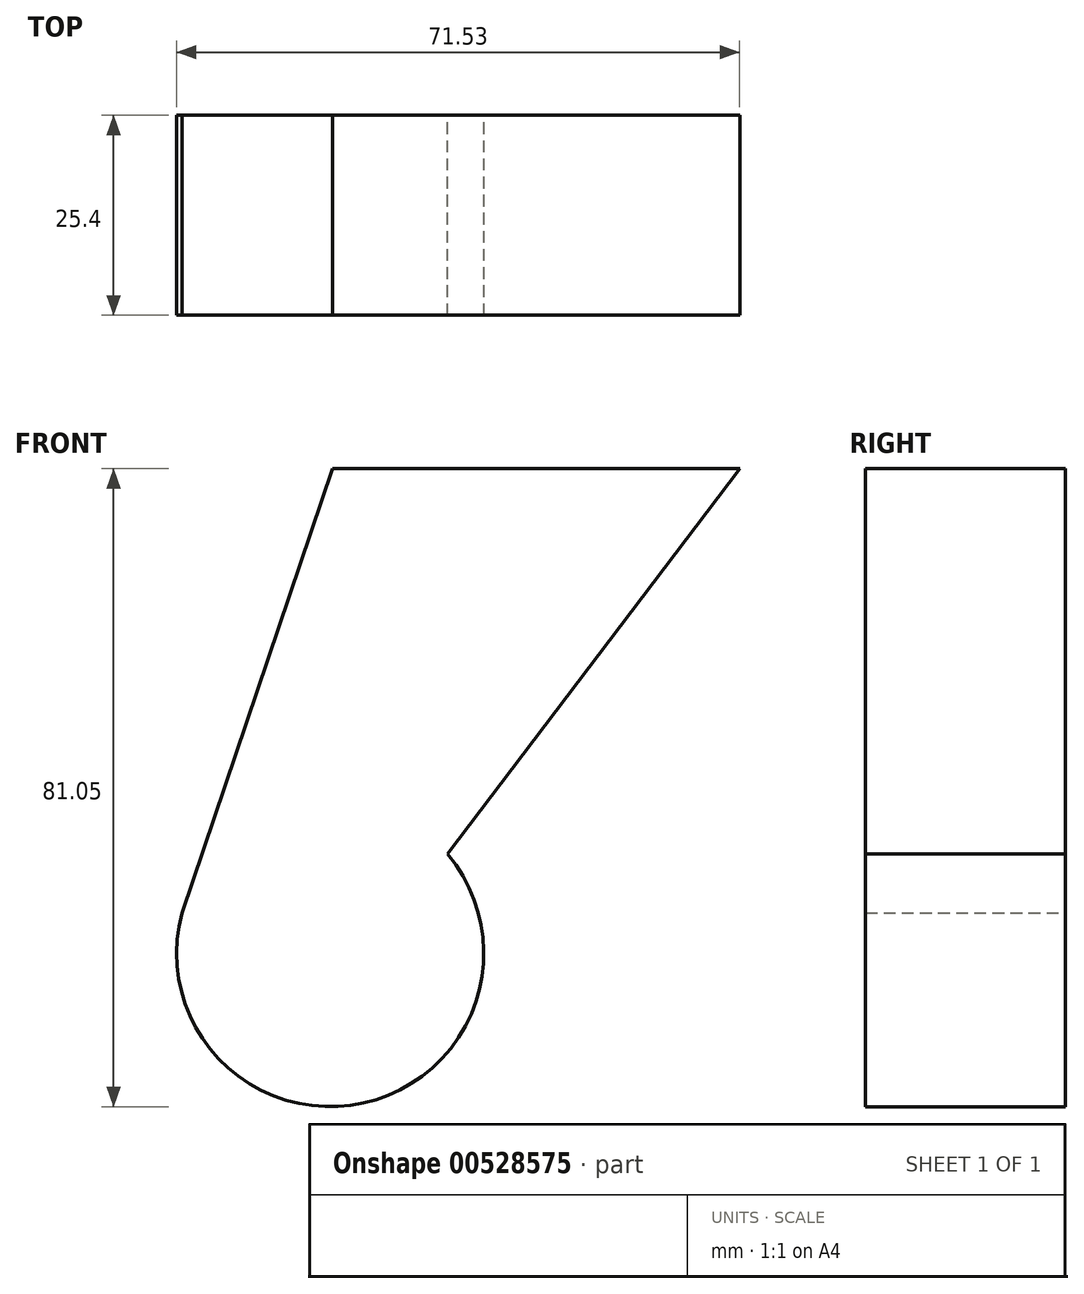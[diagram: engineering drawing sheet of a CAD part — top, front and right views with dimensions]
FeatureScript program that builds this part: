
annotation { "Feature Type Name" : "Feature", "Feature Type Description" : "" }
export const myFeature = defineFeature(function(context is Context, id is Id, definition is map)
    precondition{}
    {
        {
            var Q0;
            Q0=qCreatedBy(makeId("Front.planeOp"),FACE);
            var sketch = newSketch(context, id + "F0", { "sketchPlane" : qUnion([Q0])});
            skArc(sketch, "E0", {"start": v(-96.72, 36.47) * mm, "mid": v(-73.66, 12.33) * mm, "end": v(-62.98, 43.96) * mm});
            skLineSegment(sketch, "E1", {"start": v(-62.98, 43.96) * mm, "end": v(-25.87, 92.9) * mm});
            skLineSegment(sketch, "E2", {"start": v(-25.87, 92.9) * mm, "end": v(-77.6, 92.9) * mm});
            skLineSegment(sketch, "E3", {"start": v(-77.6, 92.9) * mm, "end": v(-96.72, 36.47) * mm});
            skSolve(sketch);
        }
        {
            var Q0;
            Q0 = qSketchRegion(id + "F0", true);
            extrude(context, id + "F1", {"entities" : qUnion([Q0]), "depth" : 25.4 * mm, "offsetDistance" : 25.4 * mm});
        }
    });
